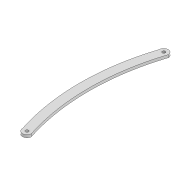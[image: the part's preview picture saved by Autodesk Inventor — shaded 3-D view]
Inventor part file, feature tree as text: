
AUTODESK INVENTOR PART (.ipt)
format: ipt  version: 2022 (Build 260153000, 153)  size: 93,696 bytes
history: native  units: mm
features: extrude x1, sketch x1
ambient origin geometry x8: Origin, YZ Plane, XZ Plane, XY Plane, X Axis, Y Axis, Z Axis, Center Point
bodies: Solid1 (feature_tree)
feature tree (2):
  extrude  "Extrusion1"  Depth=250.0mm
  sketch  "Sketch1"  dims[d0=3.3mm d1=3.3mm d2=10.0mm d3=153.584mm d6=3.0mm d7=0.0mm d12=250.0mm d13=250.0mm]
